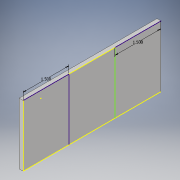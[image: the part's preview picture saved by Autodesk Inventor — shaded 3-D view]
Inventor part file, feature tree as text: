
AUTODESK INVENTOR PART (.ipt)
format: ipt  version: 2017 (Build 210142000, 142)  size: 99,328 bytes
history: native  units: in
note: dims shown in document units (in); Inventor stores cm internally (conversion verified against a paired STEP export)
features: sketch x2, extrude x1
ambient origin geometry x8: Origin, YZ Plane, XZ Plane, XY Plane, X Axis, Y Axis, Z Axis, Center Point
bodies: Solid1 (feature_tree)
feature tree (3):
  extrude  "Extrusion1"  Depth=4.5in
  sketch  "Sketch2"  dims[d2=0.125in d3=0.0in d4=1.5in d5=1.5in]
  sketch  "Sketch1"  dims[d0=2.0in d1=4.5in]
